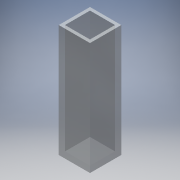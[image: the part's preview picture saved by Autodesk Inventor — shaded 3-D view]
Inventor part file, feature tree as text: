
AUTODESK INVENTOR PART (.ipt)
format: ipt  version: 2016 (Build 200138000, 138)  size: 103,936 bytes
history: native  units: mm
features: extrude x2, sketch x2
ambient origin geometry x8: Origin, YZ Plane, XZ Plane, XY Plane, X Axis, Y Axis, Z Axis, Center Point
bodies: Solid1 (feature_tree)
feature tree (4):
  extrude  "Extrusion1"  Depth=12.5mm
  extrude  "Extrusion2"  Depth=10.0mm
  sketch  "Sketch1"  dims[d0=12.5mm d1=12.5mm]
  sketch  "Sketch2"  dims[d2=45.0mm d3=0.0mm d4=10.0mm d5=10.0mm d6=1.25mm d7=1.25mm d8=43.75mm d9=0.0mm]
